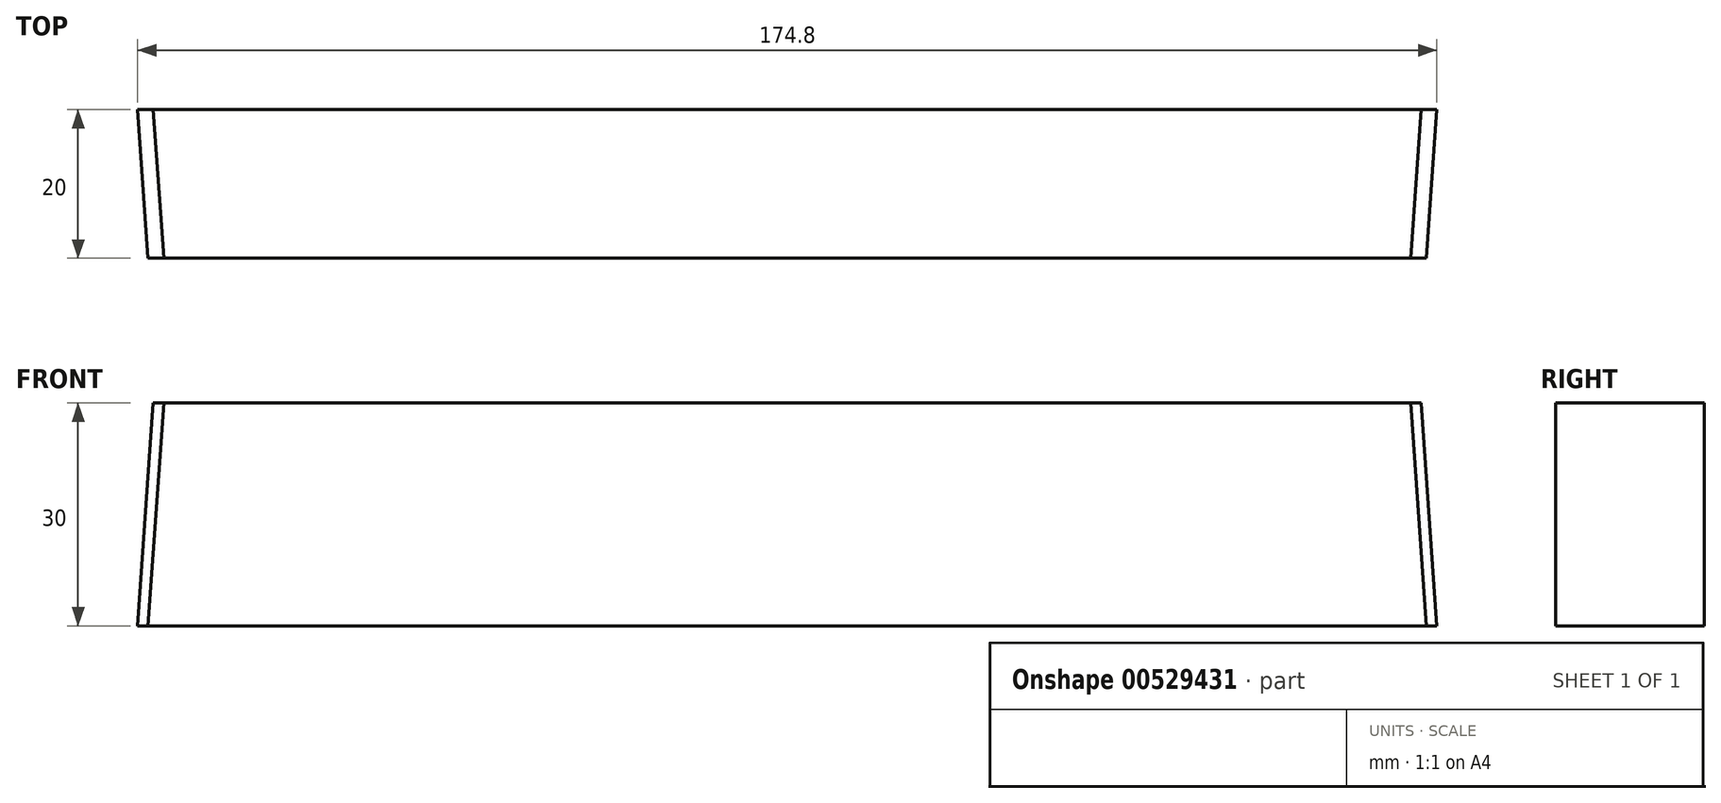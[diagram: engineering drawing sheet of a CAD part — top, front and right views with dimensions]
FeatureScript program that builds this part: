
annotation { "Feature Type Name" : "Feature", "Feature Type Description" : "" }
export const myFeature = defineFeature(function(context is Context, id is Id, definition is map)
    precondition{}
    {
        {
            var Q0;
            Q0=qCreatedBy(makeId("Top.planeOp"),FACE);
            var sketch = newSketch(context, id + "F0", { "sketchPlane" : qUnion([Q0])});
            skLineSegment(sketch, "E0", {"start": v(0, 0) * mm, "end": v(172, 0) * mm});
            skLineSegment(sketch, "E1", {"start": v(0, 0) * mm, "end": v(-7.77, 111.1) * mm, "construction": true});
            skLineSegment(sketch, "E2", {"start": v(172, 0) * mm, "end": v(178.97, 99.68) * mm, "construction": true});
            skLineSegment(sketch, "E3", {"start": v(-1.4, 20) * mm, "end": v(173.4, 20) * mm});
            skLineSegment(sketch, "E4", {"start": v(173.4, 20) * mm, "end": v(172, 0) * mm});
            skLineSegment(sketch, "E5", {"start": v(-1.4, 20) * mm, "end": v(0, 0) * mm});
            skPoint(sketch, "E6.end.orphan", {"position": v(0, 20) * mm});
            skSolve(sketch);
        }
        {
            var Q0;
            Q0 = qSketchRegion(id + "F0", true);
            extrude(context, id + "F1", {"entities" : qUnion([Q0]), "depth" : 30 * mm, "offsetDistance" : 25 * mm});
        }
        {
            var Q0;
            Q0=makeQuery(id+"F1.opExtrude","SWEPT_EDGE",EDGE,{"disambiguationData":[OSD([sQuery(id+"F0.wireOp",EDGE,"E0"),sQuery(id+"F0.wireOp",EDGE,"E5")])]});
            cPlane(context, id + "F2", {"entities" : qUnion([Q0]), "cplaneType" : CPlaneType.LINE_ANGLE, "offset" : 25 * mm, "angle" : 86 * degree, "width" : 150 * mm, "height" : 150 * mm});
        }
        {
            var Q0;
            Q0=qCreatedBy(id+"F2.planeOp",FACE);
            var sketch = newSketch(context, id + "F3", { "sketchPlane" : qUnion([Q0])});
            skLineSegment(sketch, "E7", {"start": v(0, 0) * mm, "end": v(0, 41.45) * mm, "construction": true});
            skLineSegment(sketch, "E8", {"start": v(0, 0) * mm, "end": v(-3.45, 49.38) * mm, "construction": true});
            skLineSegment(sketch, "E9", {"start": v(0, 0) * mm, "end": v(-2.5, 35.62) * mm});
            skLineSegment(sketch, "E10", {"start": v(-2.5, 35.62) * mm, "end": v(0, 35.62) * mm});
            skLineSegment(sketch, "E11", {"start": v(0, 35.62) * mm, "end": v(0, 0) * mm});
            skSolve(sketch);
        }
        {
            var Q0;
            Q0 = qSketchRegion(id + "F3", true);
            extrude(context, id + "F4", {"entities" : qUnion([Q0]), "operationType" : NewBodyOperationType.REMOVE, "endBound" : BoundingType.SYMMETRIC, "depth" : 55.4 * mm, "offsetDistance" : 25 * mm});
        }
        {
            var Q0;
            Q0=makeQuery(id+"F1.opExtrude","SWEPT_EDGE",EDGE,{"disambiguationData":[OSD([sQuery(id+"F0.wireOp",EDGE,"E0"),sQuery(id+"F0.wireOp",EDGE,"E4")])]});
            cPlane(context, id + "F5", {"entities" : qUnion([Q0]), "cplaneType" : CPlaneType.LINE_ANGLE, "offset" : 25 * mm, "angle" : 94 * degree, "width" : 150 * mm, "height" : 150 * mm});
        }
        {
            var Q0;
            Q0=qCreatedBy(id+"F5.planeOp",FACE);
            var sketch = newSketch(context, id + "F6", { "sketchPlane" : qUnion([Q0])});
            skLineSegment(sketch, "E12", {"start": v(-171.58, 0) * mm, "end": v(-171.58, 350) * mm, "construction": true});
            skLineSegment(sketch, "E13", {"start": v(-171.58, 0) * mm, "end": v(-165.32, 89.54) * mm});
            skLineSegment(sketch, "E14", {"start": v(-165.32, 89.54) * mm, "end": v(-171.58, 89.97) * mm});
            skLineSegment(sketch, "E15", {"start": v(-171.58, 89.97) * mm, "end": v(-171.58, 0) * mm});
            skSolve(sketch);
        }
        {
            var Q0;
            Q0 = qSketchRegion(id + "F6", true);
            extrude(context, id + "F7", {"entities" : qUnion([Q0]), "operationType" : NewBodyOperationType.REMOVE, "endBound" : BoundingType.SYMMETRIC, "depth" : 100.4 * mm, "offsetDistance" : 25 * mm});
        }
    });
